# Revit family: Bath-Drop_In-KOHLER-DUO-K-18775T
name_source: partatom
category: Plumbing Fixtures
units: mm (PartAtom-declared; Revit-internal decimal feet)

## family parameters
Cut with Voids When Loaded = No
Host = Face
OmniClass Number = 23.31.15.00
OmniClass Title = Bathtubs
Part Type = Normal
Room Calculation Point = No
Round Connector Dimension = Use Diameter
Shared = No

## types (2) — shared parameters
ADA Compliant = No
Assembly Code = D2010500
CW Connection = No
Cold Water Inlet = Cold Water Inlet
Date Modified = 04/01/2024
Default Elevation = 0"
Description = Doil 1.7M Acrylic Bathtub
Drain Included = No
HW Connection = No
Height = 16 3/4"
Hot Water Inlet = Hot Water Inlet
Length = 65 3/4"
Manufacturer = Kohler Co.
Master Format 2014 = 22 41 19
Master Format 2014 Name = Residential Bathtubs
Material = Cast Iron
Product Documentation Link = https://files.kohler.com.cn
Product Name = Duo
URL = http://www.kohler.com.cn
Vent Connection = No
Waste Connection = Yes
Waste Water Outlet = Waste Water Outlet
WaterSense Certified = No
Width = 29 15/16"

## per-type parameters (varying)
| type | Finish | Model | Product Page URL | Type |
| 0-White | KOHLER-Cast_Iron-0-White | K-18775T-0 | https://www.kohler.com.cn | 1 |
| 96-Biscuit | KOHLER-Enameled_Cast_Iron-96-Biscuit | K-18775T-96 |  | 2 |

## geometry (parser evidence)
native form markers: Sweep x6
no freeform markers — native parametric forms only
